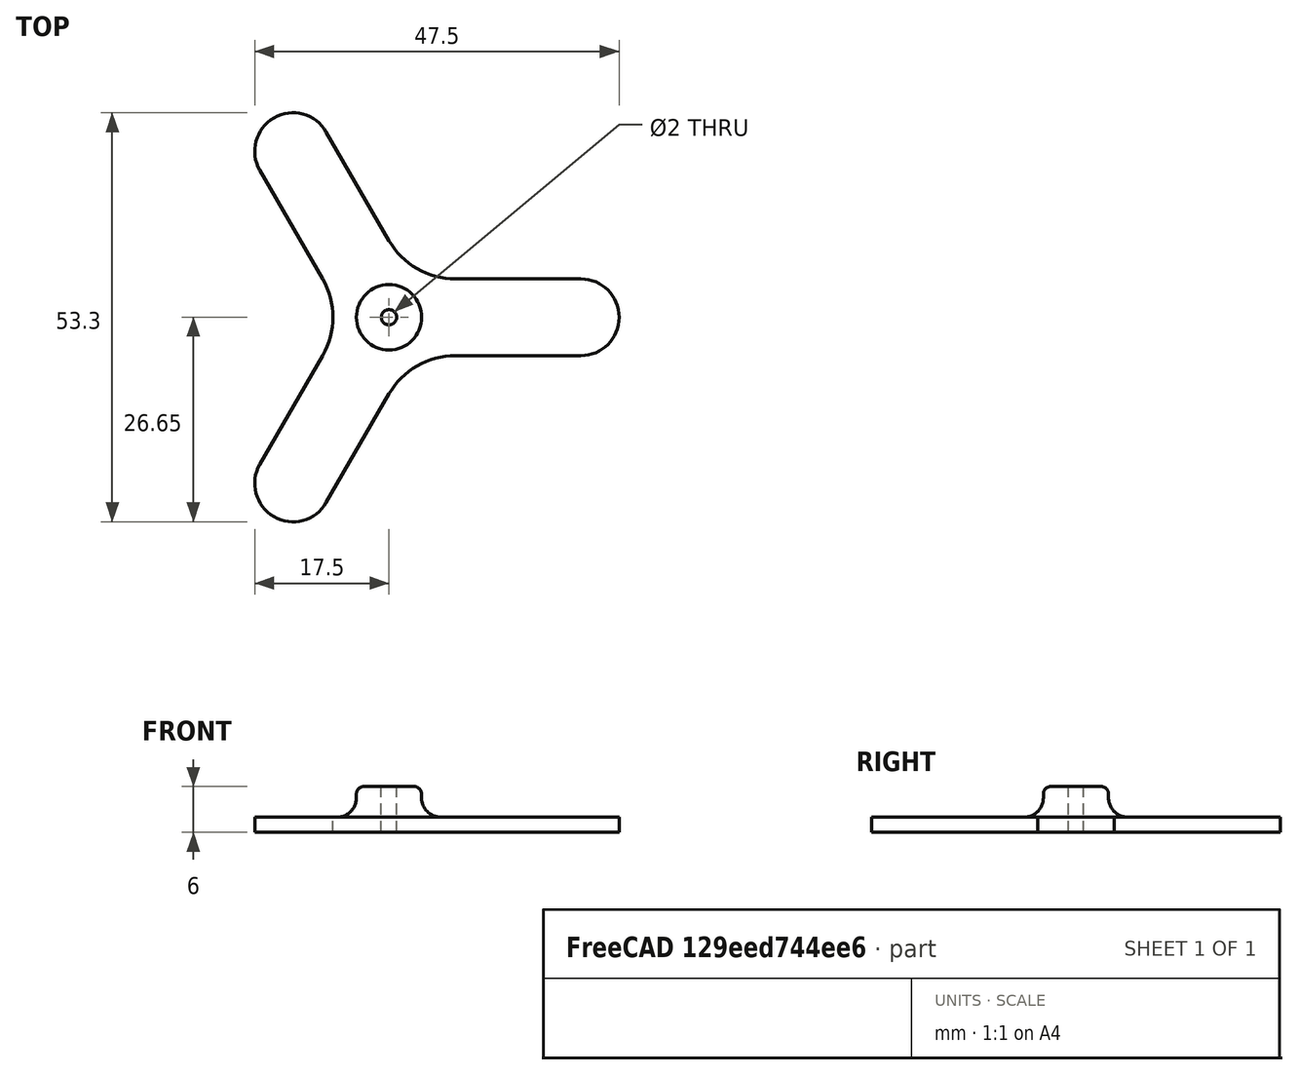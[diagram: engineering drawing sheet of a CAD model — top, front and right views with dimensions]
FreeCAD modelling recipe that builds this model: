
FCSTD DOCUMENT  (FreeCAD 0.17R13541 (Git))
Label: Pala_triple_R30mm
License: CreativeCommons Attribution
LicenseURL: http://creativecommons.org/licenses/by/4.0/
objects: Part::Cylinder×2, Part::MultiFuse×2, Part::Fillet×2, Part::Box×1, Part::FeaturePython×1, Part::Cut×1
note: 9 computed .brp shape members not serialized (recipe doc carries the construction recipe); baked Part::Feature solids carry a one-line shape summary decoded from their .brp

FEATURE [Part::Box] Box  label="pala master"
  AttacherType = Attacher::AttachEngine3D
  Height = 2
  Length = 30
  Placement = pos=(0,-5,0) rot=(0,0,1;0rad)
  Width = 10
FEATURE [Part::FeaturePython] Array  label="Array 3 palas"  # Draft array (typed FeaturePython)
  Angle = 360
  ArrayType = 1
  Axis = (0,0,1)
  Base = -> Box
  Center = (0,0,0)
  Fuse = false
  IntervalAxis = (0,0,0)
  IntervalX = (1,0,0)
  IntervalY = (0,1,0)
  IntervalZ = (0,0,0)
  NumberPolar = 3
  NumberX = 2
  NumberY = 2
  NumberZ = 1
FEATURE [Part::Cylinder] Cylinder  label="hueco eje central"
  Angle = 360
  AttacherType = Attacher::AttachEngine3D
  Height = 10
  Placement = pos=(0,0,-2) rot=(0,0,1;0rad)
  Radius = 1
FEATURE [Part::MultiFuse] Fusion  label="Conjunto de palas con radios"
  Refine = true
  Shapes = -> [Array]
FEATURE [Part::Fillet] Fillet  label="radios de acuerdo de las palas"
  Base = -> Fusion
  Edges = 9 edges: [Edge1 r=4.99,Edge3 r=4.99,Edge7 r=10,Edge10 r=10,Edge12 r=4.99,Edge15 r=4.99,Edge17 r=4.99,Edge21 r=4.99,Edge25 r=10]
FEATURE [Part::Cylinder] Cylinder001  label="Cilindro base soporte"
  Angle = 360
  AttacherType = Attacher::AttachEngine3D
  Height = 6
  Radius = 4.25
FEATURE [Part::MultiFuse] Fusion001  label="Fusion palas y soporte central"
  Refine = true
  Shapes = -> [Fillet,Cylinder001]
FEATURE [Part::Fillet] Fillet001  label="Radios palas + Base soporte"
  Base = -> Fusion001
  Edges = 2 edges: [Edge1 r=1,Edge3 r=2.5]
FEATURE [Part::Cut] Cut  label="Pala triple R30"
  Base = -> Fillet001
  Refine = true
  Tool = -> Cylinder
